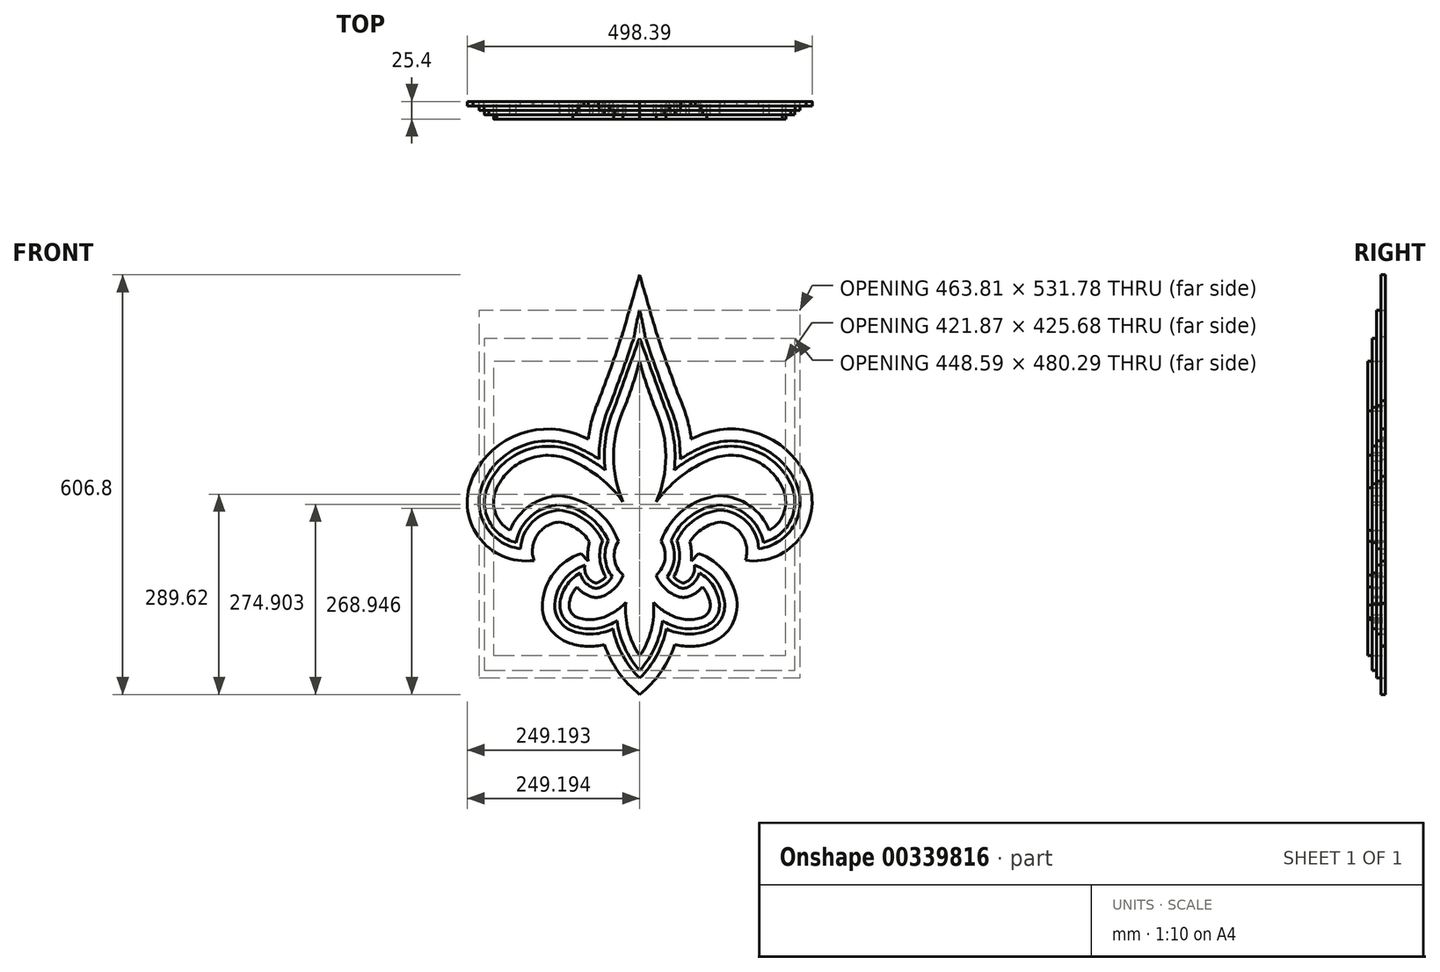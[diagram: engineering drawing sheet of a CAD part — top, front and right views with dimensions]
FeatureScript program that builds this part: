
annotation { "Feature Type Name" : "Feature", "Feature Type Description" : "" }
export const myFeature = defineFeature(function(context is Context, id is Id, definition is map)
    precondition{}
    {
        {
            var Q0;
            Q0=qCreatedBy(makeId("Front.planeOp"),FACE);
            var sketch = newSketch(context, id + "F0", { "sketchPlane" : qUnion([Q0]), "disableImprinting" : false});
            skArc(sketch, "E0", {"start": v(-22.99, -57.2) * mm, "mid": v(-28.53, -83.07) * mm, "end": v(-15.82, -106.27) * mm});
            skArc(sketch, "E1", {"start": v(-22.99, -57.2) * mm, "mid": v(-55.65, -11.85) * mm, "end": v(-107.62, 8.7) * mm});
            skArc(sketch, "E2", {"start": v(-107.62, 8.7) * mm, "mid": v(-150.9, -5.76) * mm, "end": v(-179.3, -41.48) * mm});
            skArc(sketch, "E3", {"start": v(-198.26, 20.29) * mm, "mid": v(-201.08, -14.37) * mm, "end": v(-179.3, -41.48) * mm});
            skArc(sketch, "E4", {"start": v(-88.97, 58.92) * mm, "mid": v(-151.65, 62.32) * mm, "end": v(-198.26, 20.29) * mm});
            skArc(sketch, "E5", {"start": v(-16.1, 0) * mm, "mid": v(-48.73, 34.17) * mm, "end": v(-88.97, 58.92) * mm});
            skArc(sketch, "E6", {"start": v(-16.1, 131.29) * mm, "mid": v(-29.9, 65.64) * mm, "end": v(-16.1, 0) * mm});
            skArc(sketch, "E7", {"start": v(-16.1, 131.29) * mm, "mid": v(-2.97, 166.8) * mm, "end": v(7.88, 203.07) * mm});
            skArc(sketch, "E8", {"start": v(-46.16, -136.81) * mm, "mid": v(-27.82, -124.69) * mm, "end": v(-15.82, -106.27) * mm});
            skArc(sketch, "E9", {"start": v(-63.86, -136.81) * mm, "mid": v(-55, -138.32) * mm, "end": v(-46.16, -136.81) * mm});
            skArc(sketch, "E10", {"start": v(-82.6, -123.18) * mm, "mid": v(-74.14, -131.25) * mm, "end": v(-63.86, -136.81) * mm});
            skArc(sketch, "E11", {"start": v(-82.6, -123.18) * mm, "mid": v(-90.5, -135.24) * mm, "end": v(-94.05, -149.2) * mm});
            skArc(sketch, "E12", {"start": v(-81.15, -167.83) * mm, "mid": v(-58.04, -170.2) * mm, "end": v(-35.9, -163.1) * mm});
            skArc(sketch, "E13", {"start": v(-35.9, -163.1) * mm, "mid": v(-23.05, -155.54) * mm, "end": v(-11.95, -145.56) * mm});
            skArc(sketch, "E14", {"start": v(-11.95, -145.56) * mm, "mid": v(-8.68, -185.83) * mm, "end": v(8, -222.62) * mm});
            skArc(sketch, "E15", {"start": v(-94.05, -149.2) * mm, "mid": v(-90.7, -160.66) * mm, "end": v(-81.15, -167.83) * mm});
            skPoint(sketch, "E16.orphan", {"position": v(8, -224.83) * mm});
            skArc(sketch, "E17.0", {"start": v(-24.68, -172.22) * mm, "mid": v(-13.86, -210.6) * mm, "end": v(8.02, -243.96) * mm});
            skArc(sketch, "E17.1", {"start": v(-29.88, -174.87) * mm, "mid": v(-27.25, -173.59) * mm, "end": v(-24.68, -172.22) * mm});
            skArc(sketch, "E17.2", {"start": v(-85.24, -180.39) * mm, "mid": v(-56.99, -183.37) * mm, "end": v(-29.88, -174.87) * mm});
            skArc(sketch, "E17.3", {"start": v(-107.23, -148.38) * mm, "mid": v(-101.63, -168.09) * mm, "end": v(-85.24, -180.39) * mm});
            skArc(sketch, "E17.4", {"start": v(-78.17, -103.08) * mm, "mid": v(-98.38, -122.09) * mm, "end": v(-107.23, -148.38) * mm});
            skArc(sketch, "E17.5", {"start": v(-78.17, -103.08) * mm, "mid": v(-71.35, -116.04) * mm, "end": v(-59.34, -124.4) * mm});
            skArc(sketch, "E17.6", {"start": v(-83.4, 70.9) * mm, "mid": v(-156.08, 74.76) * mm, "end": v(-210.15, 26.05) * mm});
            skArc(sketch, "E17.7", {"start": v(-41.98, 45.69) * mm, "mid": v(-61.91, 59.57) * mm, "end": v(-83.4, 70.9) * mm});
            skArc(sketch, "E17.8", {"start": v(-28.28, 136.43) * mm, "mid": v(-41.14, 91.97) * mm, "end": v(-41.98, 45.69) * mm});
            skArc(sketch, "E17.10", {"start": v(-210.15, 26.05) * mm, "mid": v(-210.77, -25.9) * mm, "end": v(-170.73, -59) * mm});
            skArc(sketch, "E17.11", {"start": v(-108, -4.54) * mm, "mid": v(-148.83, -20.87) * mm, "end": v(-170.73, -59) * mm});
            skArc(sketch, "E17.12", {"start": v(-37.5, -56.3) * mm, "mid": v(-65.69, -20.81) * mm, "end": v(-108, -4.54) * mm});
            skArc(sketch, "E17.13", {"start": v(-37.5, -56.3) * mm, "mid": v(-41.82, -83.22) * mm, "end": v(-31.71, -108.53) * mm});
            skArc(sketch, "E17.14", {"start": v(-50.77, -124.43) * mm, "mid": v(-40, -117.96) * mm, "end": v(-31.71, -108.53) * mm});
            skArc(sketch, "E17.15", {"start": v(-59.34, -124.4) * mm, "mid": v(-55.06, -125.11) * mm, "end": v(-50.77, -124.43) * mm});
            skArc(sketch, "E18", {"start": v(7.87, 236.33) * mm, "mid": v(-10.45, 186.47) * mm, "end": v(-28.28, 136.43) * mm});
            skArc(sketch, "E19.0", {"start": v(-30.52, -183.77) * mm, "mid": v(-16.56, -222.26) * mm, "end": v(8.02, -255) * mm});
            skArc(sketch, "E19.1", {"start": v(-87.6, -187.63) * mm, "mid": v(-58.69, -191.16) * mm, "end": v(-30.52, -183.77) * mm});
            skArc(sketch, "E19.2", {"start": v(-114.84, -147.9) * mm, "mid": v(-107.93, -172.37) * mm, "end": v(-87.6, -187.63) * mm});
            skArc(sketch, "E19.3", {"start": v(-71.14, -91.65) * mm, "mid": v(-101.43, -113.22) * mm, "end": v(-114.84, -147.9) * mm});
            skArc(sketch, "E19.4", {"start": v(-71.14, -91.65) * mm, "mid": v(-68.49, -107) * mm, "end": v(-56.76, -117.23) * mm});
            skArc(sketch, "E19.5", {"start": v(-80.2, 77.81) * mm, "mid": v(-158.64, 81.94) * mm, "end": v(-217, 29.37) * mm});
            skArc(sketch, "E19.6", {"start": v(-50.69, 61.45) * mm, "mid": v(-65.1, 70.24) * mm, "end": v(-80.2, 77.81) * mm});
            skArc(sketch, "E19.7", {"start": v(-35.37, 139.22) * mm, "mid": v(-47.27, 101.17) * mm, "end": v(-50.69, 61.45) * mm});
            skArc(sketch, "E19.9", {"start": v(-217, 29.37) * mm, "mid": v(-215.75, -32.95) * mm, "end": v(-164.17, -67.93) * mm});
            skArc(sketch, "E19.10", {"start": v(-108.2, -12.18) * mm, "mid": v(-146.81, -29.4) * mm, "end": v(-164.17, -67.93) * mm});
            skArc(sketch, "E19.11", {"start": v(-45.81, -56.42) * mm, "mid": v(-71.26, -26.2) * mm, "end": v(-108.2, -12.18) * mm});
            skArc(sketch, "E19.12", {"start": v(-45.81, -56.42) * mm, "mid": v(-49.51, -82.94) * mm, "end": v(-41.06, -108.35) * mm});
            skArc(sketch, "E19.13", {"start": v(-53.37, -117.26) * mm, "mid": v(-46.7, -113.52) * mm, "end": v(-41.06, -108.35) * mm});
            skArc(sketch, "E19.14", {"start": v(-56.76, -117.23) * mm, "mid": v(-55.07, -117.5) * mm, "end": v(-53.37, -117.26) * mm});
            skArc(sketch, "E20", {"start": v(-35.37, 139.22) * mm, "mid": v(-17.14, 188.65) * mm, "end": v(0, 238.47) * mm});
            skArc(sketch, "E21", {"start": v(7.86, 276.79) * mm, "mid": v(3.43, 257.73) * mm, "end": v(0, 238.47) * mm});
            skArc(sketch, "E22.0", {"start": v(-64.5, -58.16) * mm, "mid": v(-66.83, -72.04) * mm, "end": v(-66.55, -86.1) * mm});
            skArc(sketch, "E22.1", {"start": v(-64.5, -58.16) * mm, "mid": v(-83.34, -38.86) * mm, "end": v(-108.63, -29.53) * mm});
            skArc(sketch, "E22.2", {"start": v(-108.63, -29.53) * mm, "mid": v(-140.16, -48.44) * mm, "end": v(-144.78, -84.92) * mm});
            skArc(sketch, "E22.3", {"start": v(-232.55, 36.9) * mm, "mid": v(-225.2, -50.33) * mm, "end": v(-144.78, -84.92) * mm});
            skArc(sketch, "E22.4", {"start": v(-72.92, 93.48) * mm, "mid": v(-164.44, 98.2) * mm, "end": v(-232.55, 36.9) * mm});
            skArc(sketch, "E22.6", {"start": v(-51.37, 145.75) * mm, "mid": v(-33.6, 193.95) * mm, "end": v(-16.85, 242.52) * mm});
            skArc(sketch, "E22.7", {"start": v(-51.37, 145.75) * mm, "mid": v(-60.9, 118.63) * mm, "end": v(-66.47, 90.44) * mm});
            skArc(sketch, "E22.8", {"start": v(-66.47, 90.44) * mm, "mid": v(-69.68, 91.99) * mm, "end": v(-72.92, 93.48) * mm});
            skArc(sketch, "E23.0", {"start": v(-42.7, -206.72) * mm, "mid": v(-22.5, -246.36) * mm, "end": v(8.03, -278.72) * mm});
            skArc(sketch, "E23.1", {"start": v(-93.1, -204.54) * mm, "mid": v(-68.04, -209.03) * mm, "end": v(-42.7, -206.72) * mm});
            skArc(sketch, "E23.2", {"start": v(-132.58, -146.75) * mm, "mid": v(-122.65, -182.35) * mm, "end": v(-93.1, -204.54) * mm});
            skArc(sketch, "E23.3", {"start": v(-76.85, -74.82) * mm, "mid": v(-115.54, -102.4) * mm, "end": v(-132.58, -146.75) * mm});
            skLineSegment(sketch, "E24", {"start": v(-76.85, -74.82) * mm, "end": v(-66.55, -86.1) * mm});
            skArc(sketch, "E25", {"start": v(-16.85, 242.52) * mm, "mid": v(-4.5, 285.3) * mm, "end": v(7.85, 328.08) * mm});
            skArc(sketch, "E26.MirrorCS", {"start": v(72.72, -117.19) * mm, "mid": v(71.03, -117.46) * mm, "end": v(69.33, -117.23) * mm});
            skArc(sketch, "E27.MirrorCS", {"start": v(75.3, -124.36) * mm, "mid": v(71.02, -125.08) * mm, "end": v(66.73, -124.4) * mm});
            skArc(sketch, "E28.MirrorCS", {"start": v(87.08, -91.6) * mm, "mid": v(84.44, -106.95) * mm, "end": v(72.72, -117.19) * mm});
            skArc(sketch, "E29.MirrorCS", {"start": v(98.56, -123.13) * mm, "mid": v(90.1, -131.2) * mm, "end": v(79.83, -136.77) * mm});
            skArc(sketch, "E30.MirrorCS", {"start": v(69.33, -117.23) * mm, "mid": v(62.65, -113.49) * mm, "end": v(57, -108.32) * mm});
            skArc(sketch, "E31.MirrorCS", {"start": v(110.02, -149.14) * mm, "mid": v(106.68, -160.6) * mm, "end": v(97.14, -167.78) * mm});
            skArc(sketch, "E32.MirrorCS", {"start": v(79.83, -136.77) * mm, "mid": v(70.98, -138.29) * mm, "end": v(62.12, -136.78) * mm});
            skLineSegment(sketch, "E33.MirrorCS", {"start": v(92.79, -74.77) * mm, "end": v(82.49, -86.06) * mm});
            skArc(sketch, "E34.MirrorCS", {"start": v(94.12, -103.03) * mm, "mid": v(87.31, -116) * mm, "end": v(75.3, -124.36) * mm});
            skArc(sketch, "E35.MirrorCS", {"start": v(98.56, -123.13) * mm, "mid": v(106.46, -135.18) * mm, "end": v(110.02, -149.14) * mm});
            skArc(sketch, "E36.MirrorCS", {"start": v(66.73, -124.4) * mm, "mid": v(55.96, -117.93) * mm, "end": v(47.66, -108.5) * mm});
            skArc(sketch, "E37.MirrorCS", {"start": v(45.87, -174.85) * mm, "mid": v(43.24, -173.56) * mm, "end": v(40.67, -172.2) * mm});
            skArc(sketch, "E38.MirrorCS", {"start": v(82.3, 90.48) * mm, "mid": v(85.52, 92.03) * mm, "end": v(88.75, 93.53) * mm});
            skArc(sketch, "E39.MirrorCS", {"start": v(67.17, 145.78) * mm, "mid": v(76.72, 118.67) * mm, "end": v(82.3, 90.48) * mm});
            skArc(sketch, "E40.MirrorCS", {"start": v(38.9, -57.18) * mm, "mid": v(44.47, -83.04) * mm, "end": v(31.77, -106.25) * mm});
            skArc(sketch, "E41.MirrorCS", {"start": v(66.54, 61.48) * mm, "mid": v(80.95, 70.28) * mm, "end": v(96.04, 77.87) * mm});
            skArc(sketch, "E42.MirrorCS", {"start": v(123.89, -4.47) * mm, "mid": v(164.73, -20.77) * mm, "end": v(186.65, -58.9) * mm});
            skArc(sketch, "E43.MirrorCS", {"start": v(97.14, -167.78) * mm, "mid": v(74.02, -170.16) * mm, "end": v(51.9, -163.08) * mm});
            skArc(sketch, "E44.MirrorCS", {"start": v(148.56, -146.66) * mm, "mid": v(138.64, -182.27) * mm, "end": v(109.1, -204.48) * mm});
            skArc(sketch, "E45.MirrorCS", {"start": v(61.74, -56.39) * mm, "mid": v(87.16, -26.14) * mm, "end": v(124.1, -12.11) * mm});
            skArc(sketch, "E46.MirrorCS", {"start": v(103.6, -187.58) * mm, "mid": v(74.69, -191.12) * mm, "end": v(46.51, -183.75) * mm});
            skArc(sketch, "E47.MirrorCS", {"start": v(123.2, -148.31) * mm, "mid": v(117.61, -168.02) * mm, "end": v(101.24, -180.33) * mm});
            skArc(sketch, "E48.MirrorCS", {"start": v(38.9, -57.18) * mm, "mid": v(71.54, -11.81) * mm, "end": v(123.5, 8.76) * mm});
            skArc(sketch, "E49.MirrorCS", {"start": v(80.43, -58.11) * mm, "mid": v(99.25, -38.8) * mm, "end": v(124.53, -29.46) * mm});
            skArc(sketch, "E50.MirrorCS", {"start": v(99.25, 70.96) * mm, "mid": v(171.92, 74.85) * mm, "end": v(226.02, 26.17) * mm});
            skArc(sketch, "E51.MirrorCS", {"start": v(32.6, 242.54) * mm, "mid": v(20.21, 285.3) * mm, "end": v(7.85, 328.08) * mm});
            skArc(sketch, "E52.MirrorCS", {"start": v(96.04, 77.87) * mm, "mid": v(174.48, 82.03) * mm, "end": v(232.88, 29.5) * mm});
            skArc(sketch, "E53.MirrorCS", {"start": v(67.17, 145.78) * mm, "mid": v(49.37, 193.98) * mm, "end": v(32.6, 242.54) * mm});
            skArc(sketch, "E54.MirrorCS", {"start": v(87.08, -91.6) * mm, "mid": v(117.38, -113.15) * mm, "end": v(130.81, -147.82) * mm});
            skArc(sketch, "E55.MirrorCS", {"start": v(31.92, 131.3) * mm, "mid": v(45.76, 65.67) * mm, "end": v(32, 0.01) * mm});
            skArc(sketch, "E56.MirrorCS", {"start": v(27.93, -145.55) * mm, "mid": v(24.67, -185.82) * mm, "end": v(8, -222.62) * mm});
            skArc(sketch, "E57.MirrorCS", {"start": v(7.87, 236.33) * mm, "mid": v(26.22, 186.48) * mm, "end": v(44.08, 136.45) * mm});
            skArc(sketch, "E58.MirrorCS", {"start": v(40.67, -172.2) * mm, "mid": v(29.87, -210.6) * mm, "end": v(8.02, -243.96) * mm});
            skArc(sketch, "E59.MirrorCS", {"start": v(58.7, -206.7) * mm, "mid": v(38.54, -246.35) * mm, "end": v(8.03, -278.72) * mm});
            skArc(sketch, "E60.MirrorCS", {"start": v(248.42, 37.04) * mm, "mid": v(241.1, -50.2) * mm, "end": v(160.72, -84.83) * mm});
            skArc(sketch, "E61.MirrorCS", {"start": v(32, 0.01) * mm, "mid": v(64.6, 34.2) * mm, "end": v(104.82, 58.98) * mm});
            skArc(sketch, "E62.MirrorCS", {"start": v(51.18, 139.25) * mm, "mid": v(32.92, 188.67) * mm, "end": v(15.75, 238.47) * mm});
            skArc(sketch, "E63.MirrorCS", {"start": v(51.9, -163.08) * mm, "mid": v(39.03, -155.52) * mm, "end": v(27.93, -145.55) * mm});
            skArc(sketch, "E64.MirrorCS", {"start": v(31.92, 131.3) * mm, "mid": v(18.76, 166.8) * mm, "end": v(7.88, 203.07) * mm});
            skArc(sketch, "E65.MirrorCS", {"start": v(44.08, 136.45) * mm, "mid": v(56.97, 92) * mm, "end": v(57.84, 45.72) * mm});
            skArc(sketch, "E66.MirrorCS", {"start": v(62.12, -136.78) * mm, "mid": v(43.78, -124.67) * mm, "end": v(31.77, -106.25) * mm});
            skArc(sketch, "E67.MirrorCS", {"start": v(94.12, -103.03) * mm, "mid": v(114.34, -122.03) * mm, "end": v(123.2, -148.31) * mm});
            skArc(sketch, "E68.MirrorCS", {"start": v(232.88, 29.5) * mm, "mid": v(231.66, -32.82) * mm, "end": v(180.1, -67.83) * mm});
            skArc(sketch, "E69.MirrorCS", {"start": v(130.81, -147.82) * mm, "mid": v(123.92, -172.3) * mm, "end": v(103.6, -187.58) * mm});
            skArc(sketch, "E70.MirrorCS", {"start": v(124.53, -29.46) * mm, "mid": v(156.08, -48.35) * mm, "end": v(160.72, -84.83) * mm});
            skArc(sketch, "E71.MirrorCS", {"start": v(104.82, 58.98) * mm, "mid": v(167.5, 62.4) * mm, "end": v(214.14, 20.4) * mm});
            skArc(sketch, "E72.MirrorCS", {"start": v(101.24, -180.33) * mm, "mid": v(72.98, -183.33) * mm, "end": v(45.87, -174.85) * mm});
            skArc(sketch, "E73.MirrorCS", {"start": v(214.14, 20.4) * mm, "mid": v(216.97, -14.25) * mm, "end": v(195.21, -41.37) * mm});
            skArc(sketch, "E74.MirrorCS", {"start": v(88.75, 93.53) * mm, "mid": v(180.27, 98.3) * mm, "end": v(248.42, 37.04) * mm});
            skArc(sketch, "E75.MirrorCS", {"start": v(57.84, 45.72) * mm, "mid": v(77.77, 59.61) * mm, "end": v(99.25, 70.96) * mm});
            skArc(sketch, "E76.MirrorCS", {"start": v(51.18, 139.25) * mm, "mid": v(63.1, 101.2) * mm, "end": v(66.54, 61.48) * mm});
            skArc(sketch, "E77.MirrorCS", {"start": v(92.79, -74.77) * mm, "mid": v(131.49, -102.33) * mm, "end": v(148.56, -146.66) * mm});
            skArc(sketch, "E78.MirrorCS", {"start": v(226.02, 26.17) * mm, "mid": v(226.68, -25.77) * mm, "end": v(186.65, -58.9) * mm});
            skArc(sketch, "E79.MirrorCS", {"start": v(46.51, -183.75) * mm, "mid": v(32.58, -222.24) * mm, "end": v(8.02, -255) * mm});
            skArc(sketch, "E80.MirrorCS", {"start": v(61.74, -56.39) * mm, "mid": v(65.45, -82.91) * mm, "end": v(57, -108.32) * mm});
            skArc(sketch, "E81.MirrorCS", {"start": v(53.42, -56.28) * mm, "mid": v(81.59, -20.77) * mm, "end": v(123.89, -4.47) * mm});
            skArc(sketch, "E82.MirrorCS", {"start": v(80.43, -58.11) * mm, "mid": v(82.76, -72) * mm, "end": v(82.49, -86.06) * mm});
            skArc(sketch, "E83.MirrorCS", {"start": v(124.1, -12.11) * mm, "mid": v(162.72, -29.3) * mm, "end": v(180.1, -67.83) * mm});
            skArc(sketch, "E84.MirrorCS", {"start": v(109.1, -204.48) * mm, "mid": v(84.05, -208.98) * mm, "end": v(58.7, -206.7) * mm});
            skArc(sketch, "E85.MirrorCS", {"start": v(53.42, -56.28) * mm, "mid": v(57.76, -83.2) * mm, "end": v(47.66, -108.5) * mm});
            skArc(sketch, "E86.MirrorCS", {"start": v(7.86, 276.79) * mm, "mid": v(12.3, 257.73) * mm, "end": v(15.75, 238.47) * mm});
            skArc(sketch, "E87.MirrorCS", {"start": v(123.5, 8.76) * mm, "mid": v(166.8, -5.66) * mm, "end": v(195.21, -41.37) * mm});
            skSolve(sketch);
        }
        {
            var Q0;
            Q0=makeQuery(id+"F0.imprint","IMPRINT",FACE,{"disambiguationData":[TD([[makeQuery(id+"F0.imprint","IMPRINT",EDGE,{"derivedFrom":sQuery(id+"F0.wireOp",EDGE,"E0")}),1.0]])]});
            extrude(context, id + "F1", {"entities" : qUnion([Q0]), "depth" : 25.4 * mm});
        }
        {
            var Q0;
            Q0=makeQuery(id+"F0.imprint","IMPRINT",FACE,{"disambiguationData":[TD([[makeQuery(id+"F0.imprint","IMPRINT",EDGE,{"derivedFrom":sQuery(id+"F0.wireOp",EDGE,"E0")}),-1.0]])]});
            extrude(context, id + "F2", {"entities" : qUnion([Q0]), "depth" : 19.05 * mm});
        }
        {
            var Q0;
            Q0=makeQuery(id+"F0.imprint","IMPRINT",FACE,{"disambiguationData":[TD([[makeQuery(id+"F0.imprint","IMPRINT",EDGE,{"derivedFrom":sQuery(id+"F0.wireOp",EDGE,"E17.0")}),-1.0]])]});
            extrude(context, id + "F3", {"entities" : qUnion([Q0]), "depth" : 12.7 * mm});
        }
        {
            var Q0;
            Q0=makeQuery(id+"F0.imprint","IMPRINT",FACE,{"disambiguationData":[TD([[makeQuery(id+"F0.imprint","IMPRINT",EDGE,{"derivedFrom":sQuery(id+"F0.wireOp",EDGE,"E19.0")}),-1.0]])]});
            extrude(context, id + "F4", {"entities" : qUnion([Q0]), "depth" : 6.35 * mm});
        }
        {
            var Q0;
            Q0=makeQuery(id+"F3.opExtrude","SWEPT_EDGE",EDGE,{"disambiguationData":[OSD([sQuery(id+"F0.wireOp",EDGE,"E20"),sQuery(id+"F0.wireOp",EDGE,"E21")])]});
            var Q1;
            Q1=makeQuery(id+"F3.opExtrude","SWEPT_EDGE",EDGE,{"disambiguationData":[OSD([sQuery(id+"F0.wireOp",EDGE,"E62.MirrorCS"),sQuery(id+"F0.wireOp",EDGE,"E86.MirrorCS")])]});
            fillet(context, id + "F5", {"entities" : qUnion([Q0, Q1]), "radius" : 50.8 * mm, "tangentPropagation" : true, "allowEdgeOverflow" : false});
        }
        {
            var Q0;
            Q0=makeQuery(id+"F4.opExtrude","SWEPT_EDGE",EDGE,{"disambiguationData":[OSD([sQuery(id+"F0.wireOp",EDGE,"E22.6"),sQuery(id+"F0.wireOp",EDGE,"E25")])]});
            var Q1;
            Q1=makeQuery(id+"F4.opExtrude","SWEPT_EDGE",EDGE,{"disambiguationData":[OSD([sQuery(id+"F0.wireOp",EDGE,"E51.MirrorCS"),sQuery(id+"F0.wireOp",EDGE,"E53.MirrorCS")])]});
            fillet(context, id + "F6", {"entities" : qUnion([Q0, Q1]), "radius" : 50.8 * mm, "tangentPropagation" : true, "allowEdgeOverflow" : false});
        }
    });
